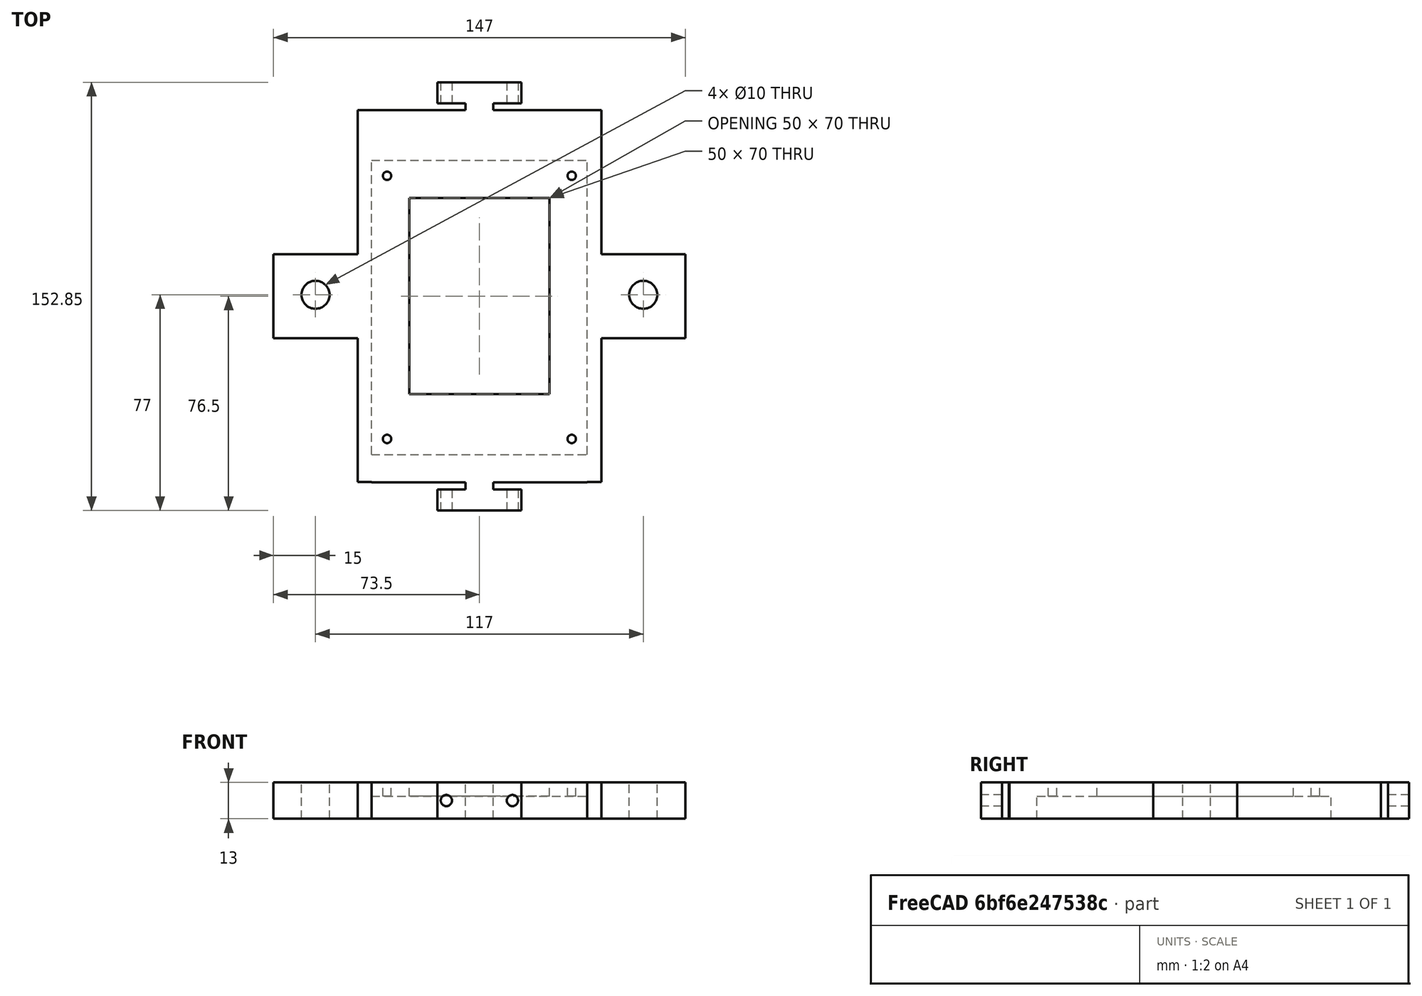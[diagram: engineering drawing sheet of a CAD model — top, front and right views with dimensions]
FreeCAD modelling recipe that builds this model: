
FCSTD DOCUMENT  (FreeCAD 0.16R6712 (Git))
Label: 2
License: All rights reserved
LicenseURL: http://en.wikipedia.org/wiki/All_rights_reserved
objects: Part::Box×14, Part::Cut×12, Part::MultiFuse×9, Part::Cylinder×9, Part::FeaturePython×2, Part::Feature×1
note: 47 computed .brp shape members not serialized (recipe doc carries the construction recipe); baked Part::Feature solids carry a one-line shape summary decoded from their .brp

FEATURE [Part::Box] Box001  label="Cubo001"
  Height = 18
  Length = 20
  Placement = pos=(12.5,20.5,0) rot=(0,0,1;0rad)
  Width = 70
FEATURE [Part::Box] Box002  label="Cubo002"
  Height = 16
  Length = 20
  Placement = pos=(42.5,20.5,0) rot=(0,0,1;0rad)
  Width = 70
FEATURE [Part::Box] Box004  label="Cubo004"
  Height = 13
  Length = 77
  Placement = pos=(-1,104,0) rot=(0,0,1;0rad)
  Width = 17.85
FEATURE [Part::Box] Box005  label="Cubo005"
  Height = 13
  Length = 77
  Placement = pos=(-1,-11,0) rot=(0,0,1;0rad)
  Width = 10
FEATURE [Part::Box] Box006  label="Cubo006"
  Height = 5
  Length = 77
  Placement = pos=(-1,-1,8) rot=(0,0,1;0rad)
  Width = 105
FEATURE [Part::Box] Box  label="Cubo"
  Height = 13
  Length = 5
  Placement = pos=(-6,-10.85,0) rot=(0,0,1;0rad)
  Width = 132.7
FEATURE [Part::Cut] Cut
  Base = -> Box006
  Tool = -> Box001
FEATURE [Part::Cut] Cut001
  Base = -> Cut
  Tool = -> Box002
FEATURE [Part::Box] Box007  label="Cubo007"
  Height = 13
  Length = 5
  Placement = pos=(76,-10.85,0) rot=(0,0,1;0rad)
  Width = 132.7
FEATURE [Part::MultiFuse] Fusion
  Shapes = -> [Cut001,Box]
FEATURE [Part::MultiFuse] Fusion001
  Shapes = -> [Box007,Fusion]
FEATURE [Part::MultiFuse] Fusion002
  Shapes = -> [Fusion001,Box004]
FEATURE [Part::MultiFuse] Fusion003
  Shapes = -> [Box005,Fusion002]
FEATURE [Part::Box] Box008  label="Cubo008"
  Height = 13
  Length = 30
  Placement = pos=(22.5,-21,0) rot=(0,0,1;0rad)
  Width = 10
FEATURE [Part::FeaturePython] Array  # Draft array (typed FeaturePython)
  Angle = 360
  ArrayType = 0
  Axis = (0,0,1)
  Base = -> Box008
  Center = (0,0,0)
  Fuse = false
  IntervalAxis = (0,0,0)
  IntervalX = (1,0,0)
  IntervalY = (0,142.85,0)
  IntervalZ = (0,0,0)
  NumberPolar = 1
  NumberX = 1
  NumberY = 2
  NumberZ = 1
FEATURE [Part::Box] Box009  label="Cubo009"
  Height = 10
  Length = 17
  Placement = pos=(28,20.5,4) rot=(0,0,1;0rad)
  Width = 70
FEATURE [Part::Cut] Cut002
  Base = -> Fusion003
  Tool = -> Box009
FEATURE [Part::Box] Box010  label="Cubo010"
  Height = 13
  Length = 30
  Placement = pos=(-36,40.5,0) rot=(0,0,1;0rad)
  Width = 30
FEATURE [Part::Cylinder] Cylinder  label="Cilindro"
  Angle = 360
  Height = 13
  Placement = pos=(-21,56,0) rot=(0,0,1;0rad)
  Radius = 5
FEATURE [Part::Cut] Cut003
  Base = -> Box010
  Tool = -> Cylinder
FEATURE [Part::FeaturePython] Array001  # Draft array (typed FeaturePython)
  Angle = 360
  ArrayType = 0
  Axis = (0,0,1)
  Base = -> Cut003
  Center = (0,0,0)
  Fuse = false
  IntervalAxis = (0,0,0)
  IntervalX = (117,0,0)
  IntervalY = (0,1,0)
  IntervalZ = (0,0,0)
  NumberPolar = 1
  NumberX = 2
  NumberY = 1
  NumberZ = 1
FEATURE [Part::Box] Box011  label="Cubo011"
  Height = 13
  Length = 10
  Placement = pos=(22.5,-13.5,0) rot=(0,0,1;0rad)
  Width = 2.5
FEATURE [Part::Cylinder] Cylinder001  label="Cilindro001"
  Angle = 360
  Height = 10
  Placement = pos=(25.7,-11,6.5) rot=(1,0,0;1.5708rad)
  Radius = 2
FEATURE [Part::MultiFuse] Fusion004
  Shapes = -> [Cylinder001,Box011]
FEATURE [Part::Cut] Cut004
  Base = -> Array
  Tool = -> Fusion004
FEATURE [Part::Box] Box012  label="Cubo012"
  Height = 13
  Length = 10
  Placement = pos=(42.5,-13.5,0) rot=(0,0,1;0rad)
  Width = 2.5
FEATURE [Part::Cylinder] Cylinder002  label="Cilindro002"
  Angle = 360
  Height = 10
  Placement = pos=(49.3,-11,6.5) rot=(1,0,0;1.5708rad)
  Radius = 2
FEATURE [Part::MultiFuse] Fusion005
  Shapes = -> [Cylinder002,Box012]
FEATURE [Part::Cut] Cut005
  Base = -> Cut004
  Tool = -> Fusion005
FEATURE [Part::Box] Box013  label="Cubo013"
  Height = 13
  Length = 10
  Placement = pos=(22.5,121.85,0) rot=(0,0,1;0rad)
  Width = 2.5
FEATURE [Part::Cylinder] Cylinder003  label="Cilindro003"
  Angle = 360
  Height = 10
  Placement = pos=(25.7,131.85,6.5) rot=(1,0,0;1.5708rad)
  Radius = 2
FEATURE [Part::Box] Box014  label="Cubo014"
  Height = 13
  Length = 10
  Placement = pos=(42.5,121.85,0) rot=(0,0,1;0rad)
  Width = 2.5
FEATURE [Part::Cylinder] Cylinder004  label="Cilindro004"
  Angle = 360
  Height = 10
  Placement = pos=(49.3,131.85,6.5) rot=(1,0,0;1.5708rad)
  Radius = 2
FEATURE [Part::MultiFuse] Fusion006
  Shapes = -> [Cylinder004,Box014]
FEATURE [Part::MultiFuse] Fusion007
  Shapes = -> [Cylinder003,Box013]
FEATURE [Part::Cut] Cut006
  Base = -> Cut005
  Tool = -> Fusion006
FEATURE [Part::Cut] Cut007
  Base = -> Cut006
  Tool = -> Fusion007
FEATURE [Part::MultiFuse] Fusion008
  Shapes = -> [Cut002,Cut007,Array001]
FEATURE [Part::Cylinder] Cylinder005  label="Cilindro005"
  Angle = 360
  Height = 10
  Placement = pos=(4.55,4.55,5) rot=(0,0,1;0rad)
  Radius = 1.5
FEATURE [Part::Cut] Cut008
  Base = -> Fusion008
  Tool = -> Cylinder005
FEATURE [Part::Cylinder] Cylinder006  label="Cilindro006"
  Angle = 360
  Height = 10
  Placement = pos=(70.45,4.55,6) rot=(0,0,1;0rad)
  Radius = 1.5
FEATURE [Part::Cut] Cut009
  Base = -> Cut008
  Tool = -> Cylinder006
FEATURE [Part::Cylinder] Cylinder007  label="Cilindro007"
  Angle = 360
  Height = 10
  Placement = pos=(4.55,98.45,4) rot=(0,0,1;0rad)
  Radius = 1.5
FEATURE [Part::Cut] Cut010
  Base = -> Cut009
  Tool = -> Cylinder007
FEATURE [Part::Cylinder] Cylinder008  label="Cilindro008"
  Angle = 360
  Height = 10
  Placement = pos=(70.45,98.45,5) rot=(0,0,1;0rad)
  Radius = 1.5
FEATURE [Part::Cut] Cut011
  Base = -> Cut010
  Tool = -> Cylinder008
FEATURE [Part::Feature] Cut011001  label="Cut012"
  shape: bbox 147 x 152.9 x 13 mm, 53 faces (baked)
